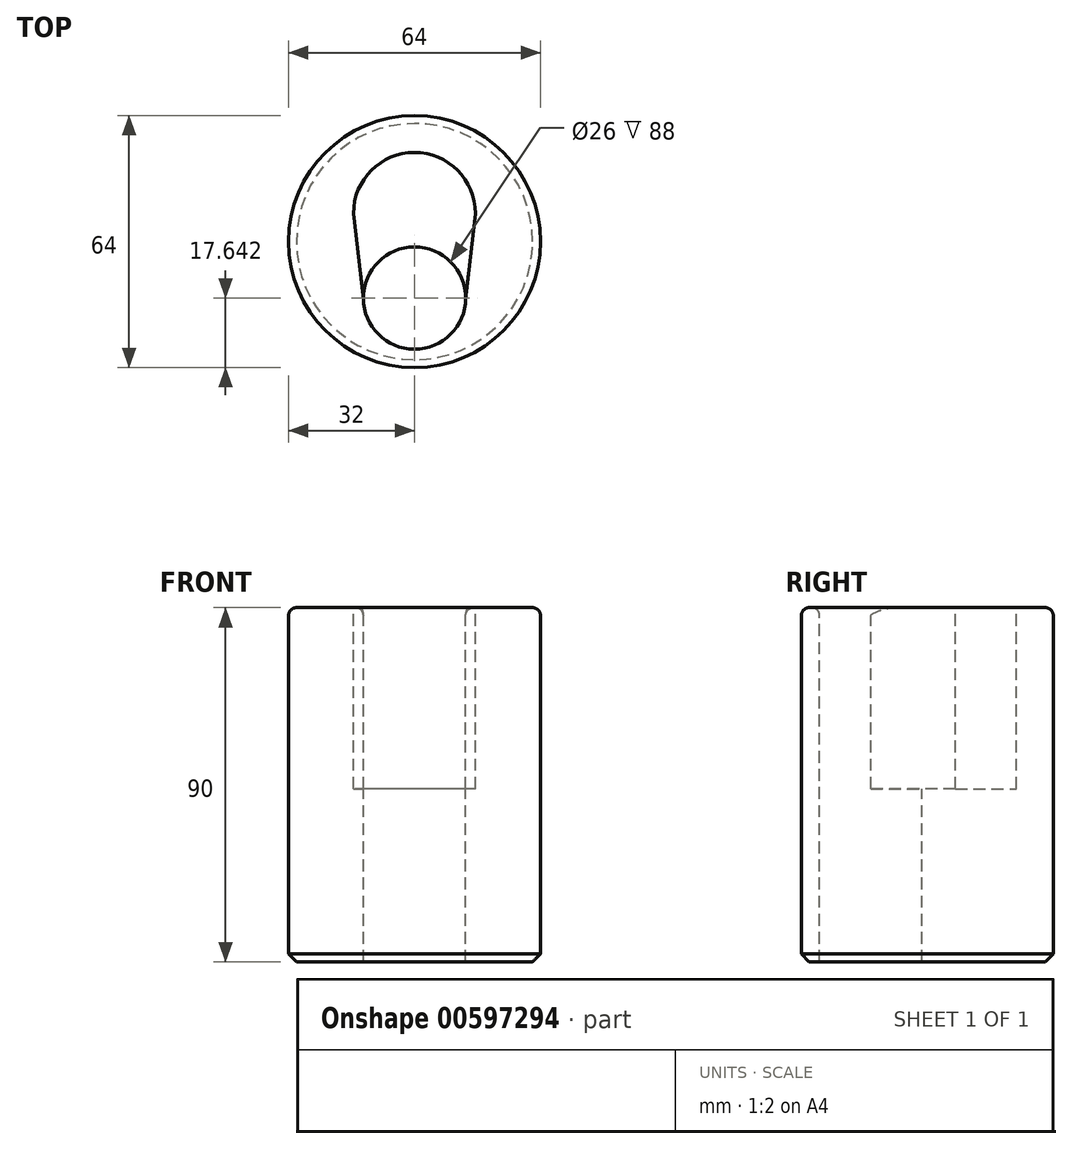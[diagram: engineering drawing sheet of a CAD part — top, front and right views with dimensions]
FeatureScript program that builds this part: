
annotation { "Feature Type Name" : "Feature", "Feature Type Description" : "" }
export const myFeature = defineFeature(function(context is Context, id is Id, definition is map)
    precondition{}
    {
        {
            var Q0;
            Q0=qCreatedBy(makeId("Top.planeOp"),FACE);
            var sketch = newSketch(context, id + "F0", { "sketchPlane" : qUnion([Q0])});
            skCircle(sketch, "E0", {"center": v(0, 0) * mm, "radius": 32 * mm});
            skLineSegment(sketch, "E1", {"start": v(-32, 0) * mm, "end": v(32, 0) * mm, "construction": true});
            skLineSegment(sketch, "E2", {"start": v(0, -32) * mm, "end": v(0, 32) * mm, "construction": true});
            skCircle(sketch, "E3", {"center": v(0, -14.36) * mm, "radius": 13 * mm});
            skLineSegment(sketch, "E4", {"start": v(-15.5, 7.14) * mm, "end": v(15.5, 7.14) * mm, "construction": true});
            skLineSegment(sketch, "E5", {"start": v(-13, -14.36) * mm, "end": v(13, -14.36) * mm, "construction": true});
            skLineSegment(sketch, "E6", {"start": v(-15.5, 7.14) * mm, "end": v(-13, -14.36) * mm});
            skLineSegment(sketch, "E7", {"start": v(15.5, 7.14) * mm, "end": v(13, -14.36) * mm});
            skArc(sketch, "E8.trimOffspring", {"start": v(15.5, 7.14) * mm, "mid": v(0, 22.64) * mm, "end": v(-15.5, 7.14) * mm});
            skPoint(sketch, "E9", {"position": v(0, 22.64) * mm});
            skPoint(sketch, "E10", {"position": v(0, -27.36) * mm});
            skSolve(sketch);
        }
        {
            var Q0;
            Q0 = qSketchRegion(id + "F0", true);
            var Q1;
            {var subQ0=sQuery(id+"F0.wireOp",EDGE,"J50kX6nI-z2BG-bCxQ-QFYg-jqEeVpyUEYx6");var subQ1=sQuery(id+"F0.wireOp",EDGE,"E3");var subQ5=makeQuery(id+"F0.imprint","INTERSECT",VERTEX,{"disambiguationData":[OD(1.0)],"derivedFrom":[subQ1,subQ0]});Q1=makeQuery(id+"F0.imprint","IMPRINT",FACE,{"disambiguationData":[TD([[makeQuery(id+"F0.imprint","IMPRINT",EDGE,{"disambiguationData":[TD([[subQ5,1.0]])],"derivedFrom":subQ1}),-1.0]])]});}
            extrude(context, id + "F1", {"entities" : qUnion([Q0, Q1]), "oppositeDirection" : true, "depth" : 90 * mm, "offsetDistance" : 25 * mm});
        }
        {
            var Q0;
            {var subQ3=sQuery(id+"F0.wireOp",EDGE,"E6");Q0=makeQuery(id+"F0.imprint","IMPRINT",FACE,{"disambiguationData":[TD([[makeQuery(id+"F0.imprint","IMPRINT",EDGE,{"derivedFrom":subQ3}),1.0]])]});}
            extrude(context, id + "F2", {"entities" : qUnion([Q0]), "operationType" : NewBodyOperationType.REMOVE, "oppositeDirection" : true, "depth" : 46 * mm, "offsetDistance" : 25 * mm});
        }
        {
            var Q0;
            Q0=makeQuery(id+"F2.boolean.opBoolean","COPY",EDGE,{"derivedFrom":makeQuery(id+"F2.opExtrude","CAP_EDGE",EDGE,{"disambiguationData":[OSD([sQuery(id+"F0.wireOp",EDGE,"E6")])],"isStart":true})});
            var Q1;
            Q1=makeQuery(id+"F2.boolean.opBoolean","COPY",EDGE,{"derivedFrom":makeQuery(id+"F2.opExtrude","CAP_EDGE",EDGE,{"disambiguationData":[OSD([sQuery(id+"F0.wireOp",EDGE,"E8.trimOffspring")])],"isStart":true})});
            var Q2;
            Q2=makeQuery(id+"F1.opExtrude","CAP_EDGE",EDGE,{"disambiguationData":[OSD([sQuery(id+"F0.wireOp",EDGE,"E3")])],"isStart":true});
            var Q3;
            Q3=makeQuery(id+"F2.boolean.opBoolean","COPY",EDGE,{"derivedFrom":makeQuery(id+"F2.opExtrude","CAP_EDGE",EDGE,{"disambiguationData":[OSD([sQuery(id+"F0.wireOp",EDGE,"E7")])],"isStart":true})});
            fillet(context, id + "F3", {"entities" : qUnion([Q0, Q1, Q2, Q3]), "radius" : 2 * mm, "tangentPropagation" : true, "allowEdgeOverflow" : false});
        }
        {
            var Q0;
            Q0=makeQuery(id+"F1.opExtrude","CAP_EDGE",EDGE,{"disambiguationData":[OSD([sQuery(id+"F0.wireOp",EDGE,"E0")])],"isStart":true});
            fillet(context, id + "F4", {"entities" : qUnion([Q0]), "radius" : 2 * mm, "tangentPropagation" : true, "allowEdgeOverflow" : false});
        }
        {
            var Q0;
            Q0=makeQuery(id+"F1.opExtrude","CAP_EDGE",EDGE,{"disambiguationData":[OSD([sQuery(id+"F0.wireOp",EDGE,"E0")])],"isStart":false});
            chamfer(context, id + "F5", {"entities" : qUnion([Q0]), "width" : 2 * mm, "tangentPropagation" : true});
        }
    });
